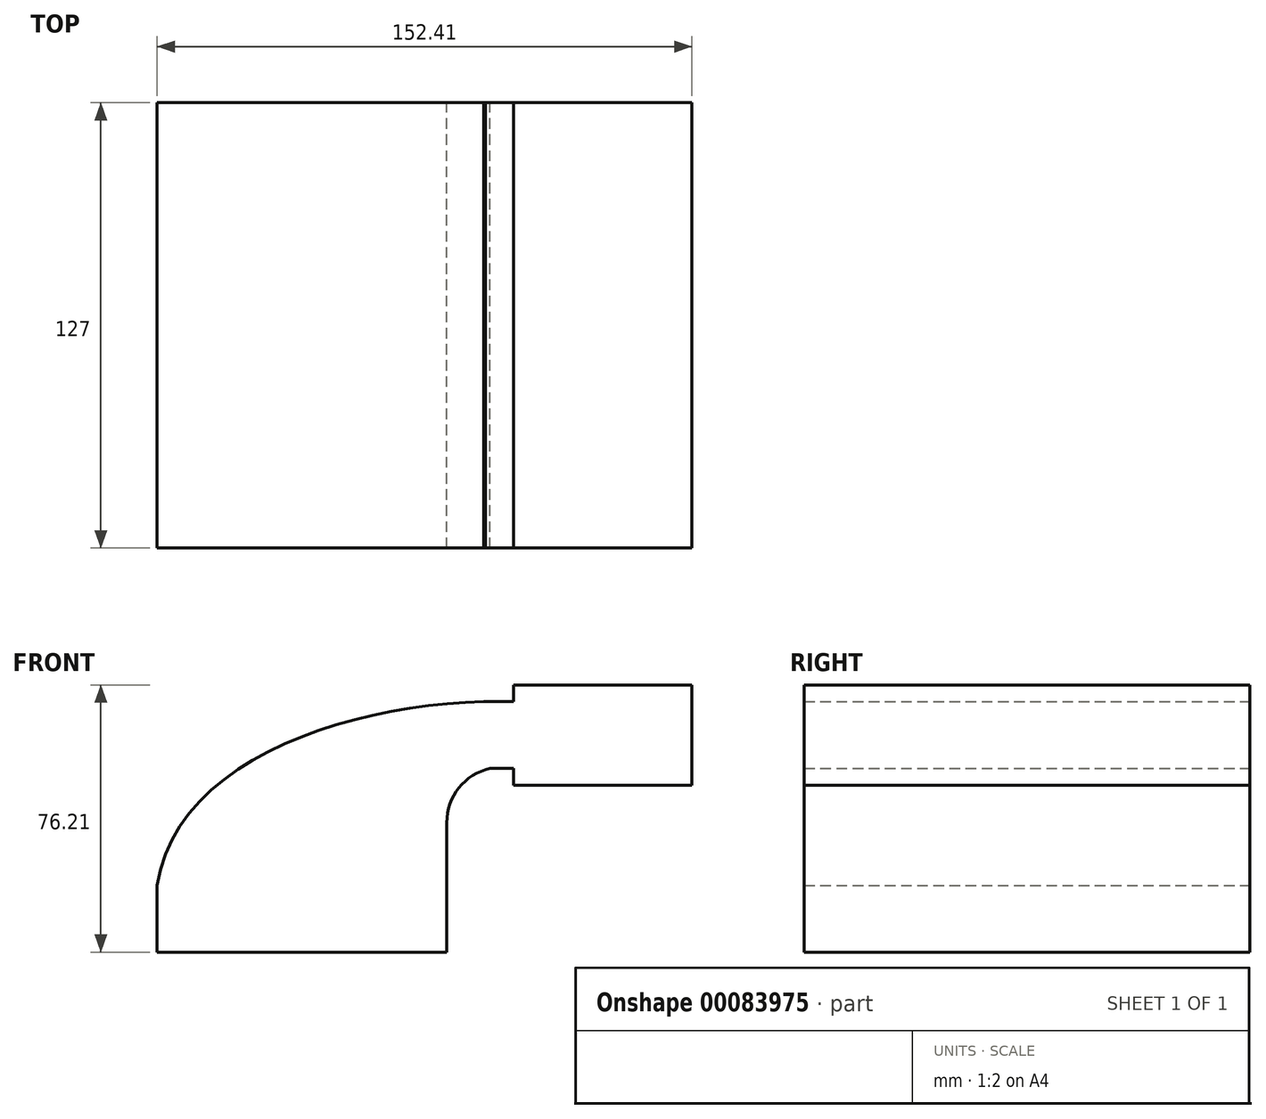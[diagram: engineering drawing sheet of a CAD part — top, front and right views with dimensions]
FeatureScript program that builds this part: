
annotation { "Feature Type Name" : "Feature", "Feature Type Description" : "" }
export const myFeature = defineFeature(function(context is Context, id is Id, definition is map)
    precondition{}
    {
        {
            var Q0;
            Q0=qCreatedBy(makeId("Front.planeOp"),FACE);
            var sketch = newSketch(context, id + "F0", { "sketchPlane" : qUnion([Q0])});
            skLineSegment(sketch, "E0.bottom", {"start": v(-41.28, 9.52) * mm, "end": v(41.28, 9.53) * mm});
            skLineSegment(sketch, "E0.top", {"start": v(-41.28, -9.53) * mm, "end": v(41.28, -9.53) * mm});
            skLineSegment(sketch, "E0.left", {"start": v(-41.28, 9.52) * mm, "end": v(-41.28, -9.53) * mm});
            skLineSegment(sketch, "E0.right", {"start": v(41.28, 9.53) * mm, "end": v(41.28, -9.52) * mm});
            skPoint(sketch, "E0.middle", {"position": v(0, 0) * mm});
            skLineSegment(sketch, "E1.bottom", {"start": v(111.12, 38.1) * mm, "end": v(60.32, 38.1) * mm});
            skLineSegment(sketch, "E1.top", {"start": v(111.12, 66.67) * mm, "end": v(60.32, 66.67) * mm});
            skLineSegment(sketch, "E1.left", {"start": v(111.12, 38.1) * mm, "end": v(111.12, 66.67) * mm});
            skLineSegment(sketch, "E1.right", {"start": v(60.32, 38.1) * mm, "end": v(60.32, 66.68) * mm});
            skPoint(sketch, "E1.middle", {"position": v(85.72, 52.39) * mm});
            skLineSegment(sketch, "E2", {"start": v(41.27, 9.53) * mm, "end": v(41.27, 27.4) * mm});
            skArc(sketch, "E3", {"start": v(41.27, 27.4) * mm, "mid": v(44.72, 37.29) * mm, "end": v(53.57, 42.88) * mm});
            skLineSegment(sketch, "E4", {"start": v(53.57, 42.88) * mm, "end": v(85.68, 42.88) * mm});
            skLineSegment(sketch, "E5.0", {"start": v(51.82, 61.93) * mm, "end": v(85.68, 61.93) * mm});
            skArc(sketch, "E5.1", {"start": v(22.22, 27.4) * mm, "mid": v(30.64, 50.14) * mm, "end": v(51.82, 61.93) * mm});
            skLineSegment(sketch, "E5.2", {"start": v(22.22, 9.53) * mm, "end": v(22.22, 27.4) * mm});
            skLineSegment(sketch, "E6", {"start": v(85.68, 42.88) * mm, "end": v(85.68, 61.93) * mm});
            skFitSpline(sketch, "E7", {"points": [v(-41.28, 9.53) * mm, v(60.32, 61.93) * mm], "startDerivative": vector(17.7, 115.44) * mm, "endDerivative": vector(120.62, -3.17) * mm});
            skSolve(sketch);
        }
        {
            var Q0;
            Q0 = qSketchRegion(id + "F0", true);
            extrude(context, id + "F1", {"entities" : qUnion([Q0]), "endBound" : BoundingType.SYMMETRIC, "depth" : 127 * mm});
        }
    });
